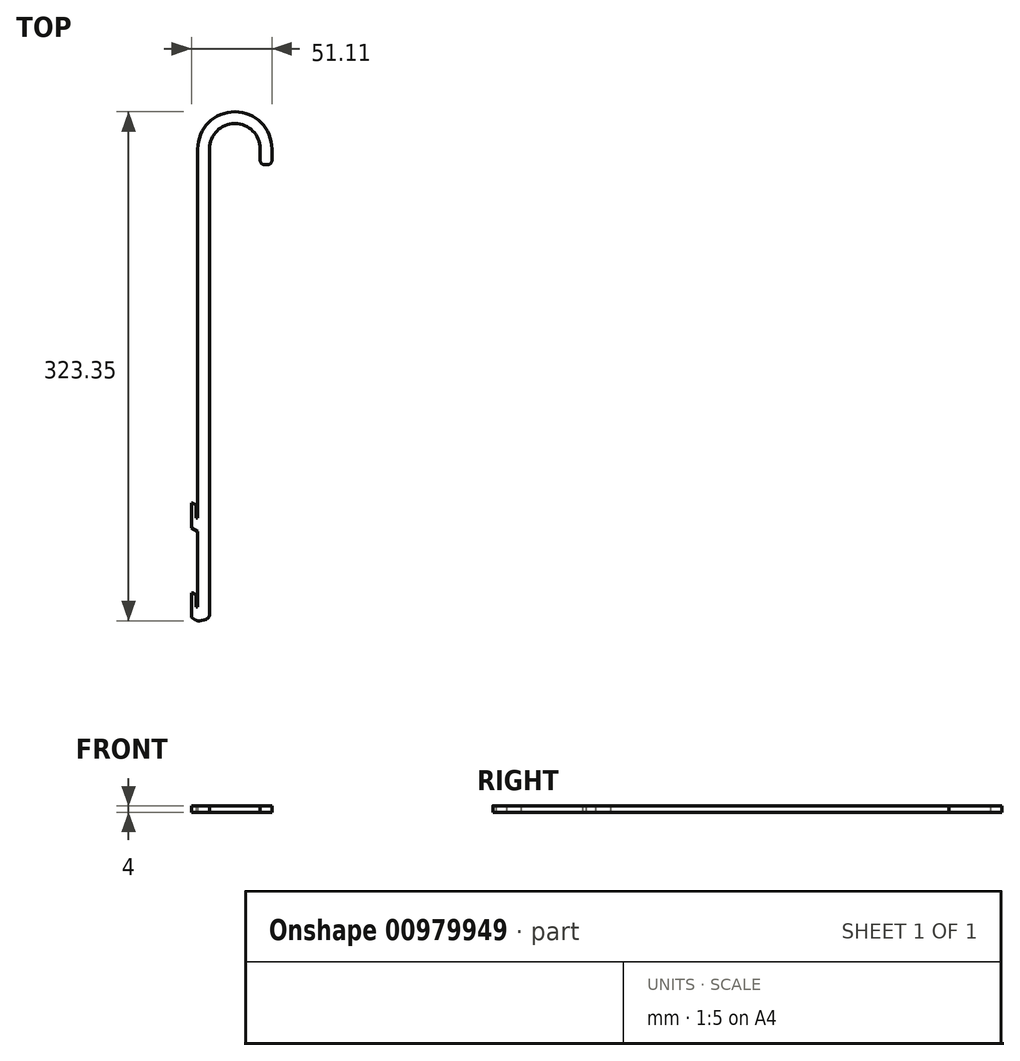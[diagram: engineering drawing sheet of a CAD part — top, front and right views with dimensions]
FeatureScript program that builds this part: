
annotation { "Feature Type Name" : "Feature", "Feature Type Description" : "" }
export const myFeature = defineFeature(function(context is Context, id is Id, definition is map)
    precondition{}
    {
        {
            var Q0;
            Q0=qCreatedBy(makeId("Top.planeOp"),FACE);
            var sketch = newSketch(context, id + "F0", { "sketchPlane" : qUnion([Q0])});
            skLineSegment(sketch, "E0", {"start": v(-12.62, -16.07) * mm, "end": v(-12.62, -7.05) * mm});
            skLineSegment(sketch, "E1", {"start": v(-12.62, -7.05) * mm, "end": v(-15.64, -7.05) * mm});
            skLineSegment(sketch, "E2", {"start": v(-15.64, -7.05) * mm, "end": v(-15.64, -22.73) * mm});
            skLineSegment(sketch, "E3", {"start": v(-15.64, -22.73) * mm, "end": v(-11.62, -25.05) * mm});
            skLineSegment(sketch, "E4", {"start": v(-11.62, 31.95) * mm, "end": v(-11.62, -16.07) * mm});
            skLineSegment(sketch, "E5", {"start": v(-11.62, -16.07) * mm, "end": v(-12.62, -16.07) * mm});
            skLineSegment(sketch, "E6", {"start": v(-11.62, 31.95) * mm, "end": v(-15.64, 34.27) * mm});
            skLineSegment(sketch, "E7", {"start": v(-15.64, 34.27) * mm, "end": v(-15.64, 49.95) * mm});
            skLineSegment(sketch, "E8", {"start": v(-15.64, 49.95) * mm, "end": v(-12.62, 49.95) * mm});
            skLineSegment(sketch, "E9", {"start": v(-12.62, 49.95) * mm, "end": v(-12.62, 40.39) * mm});
            skLineSegment(sketch, "E10", {"start": v(-12.62, 40.39) * mm, "end": v(-11.62, 40.39) * mm});
            skLineSegment(sketch, "E11", {"start": v(-11.62, 40.39) * mm, "end": v(-11.62, 274.95) * mm});
            skLineSegment(sketch, "E12", {"start": v(-11.62, -25.05) * mm, "end": v(-4.16, -23.27) * mm});
            skLineSegment(sketch, "E13", {"start": v(-4.16, -23.27) * mm, "end": v(-4.16, 274.95) * mm});
            skLineSegment(sketch, "E14", {"start": v(-4.16, 274.95) * mm, "end": v(-11.62, 274.95) * mm});
            skArc(sketch, "E15", {"start": v(28.01, 274.95) * mm, "mid": v(11.92, 291.04) * mm, "end": v(-4.16, 274.95) * mm});
            skArc(sketch, "E16", {"start": v(-11.62, 274.95) * mm, "mid": v(11.92, 298.5) * mm, "end": v(35.47, 274.95) * mm});
            skLineSegment(sketch, "E17", {"start": v(28.01, 274.95) * mm, "end": v(28.01, 264.83) * mm});
            skLineSegment(sketch, "E18", {"start": v(28.01, 264.83) * mm, "end": v(35.47, 264.83) * mm});
            skLineSegment(sketch, "E19", {"start": v(35.47, 264.83) * mm, "end": v(35.47, 274.95) * mm});
            skSolve(sketch);
        }
        {
            var Q0;
            Q0 = qSketchRegion(id + "F0", true);
            extrude(context, id + "F1", {"entities" : qUnion([Q0]), "endBound" : BoundingType.SYMMETRIC, "depth" : 4 * mm, "offsetDistance" : 25 * mm});
        }
        {
            var Q0;
            Q0=makeQuery(id+"F1.opExtrude","SWEPT_EDGE",EDGE,{"disambiguationData":[OSD([sQuery(id+"F0.wireOp",EDGE,"E17"),sQuery(id+"F0.wireOp",EDGE,"E18")])]});
            var Q1;
            Q1=makeQuery(id+"F1.opExtrude","SWEPT_EDGE",EDGE,{"disambiguationData":[OSD([sQuery(id+"F0.wireOp",EDGE,"E18"),sQuery(id+"F0.wireOp",EDGE,"E19")])]});
            var Q2;
            Q2=makeQuery(id+"F1.opExtrude","SWEPT_EDGE",EDGE,{"disambiguationData":[OSD([sQuery(id+"F0.wireOp",EDGE,"E12"),sQuery(id+"F0.wireOp",EDGE,"E13")])]});
            var Q3;
            Q3=makeQuery(id+"F1.opExtrude","SWEPT_EDGE",EDGE,{"disambiguationData":[OSD([sQuery(id+"F0.wireOp",EDGE,"E3"),sQuery(id+"F0.wireOp",EDGE,"E12")])]});
            var Q4;
            Q4=makeQuery(id+"F1.opExtrude","SWEPT_EDGE",EDGE,{"disambiguationData":[OSD([sQuery(id+"F0.wireOp",EDGE,"E8"),sQuery(id+"F0.wireOp",EDGE,"E9")])]});
            var Q5;
            Q5=makeQuery(id+"F1.opExtrude","SWEPT_EDGE",EDGE,{"disambiguationData":[OSD([sQuery(id+"F0.wireOp",EDGE,"E0"),sQuery(id+"F0.wireOp",EDGE,"E1")])]});
            fillet(context, id + "F2", {"entities" : qUnion([Q0, Q1, Q2, Q3, Q4, Q5]), "radius" : 3 * mm, "tangentPropagation" : true, "allowEdgeOverflow" : false});
        }
    });
